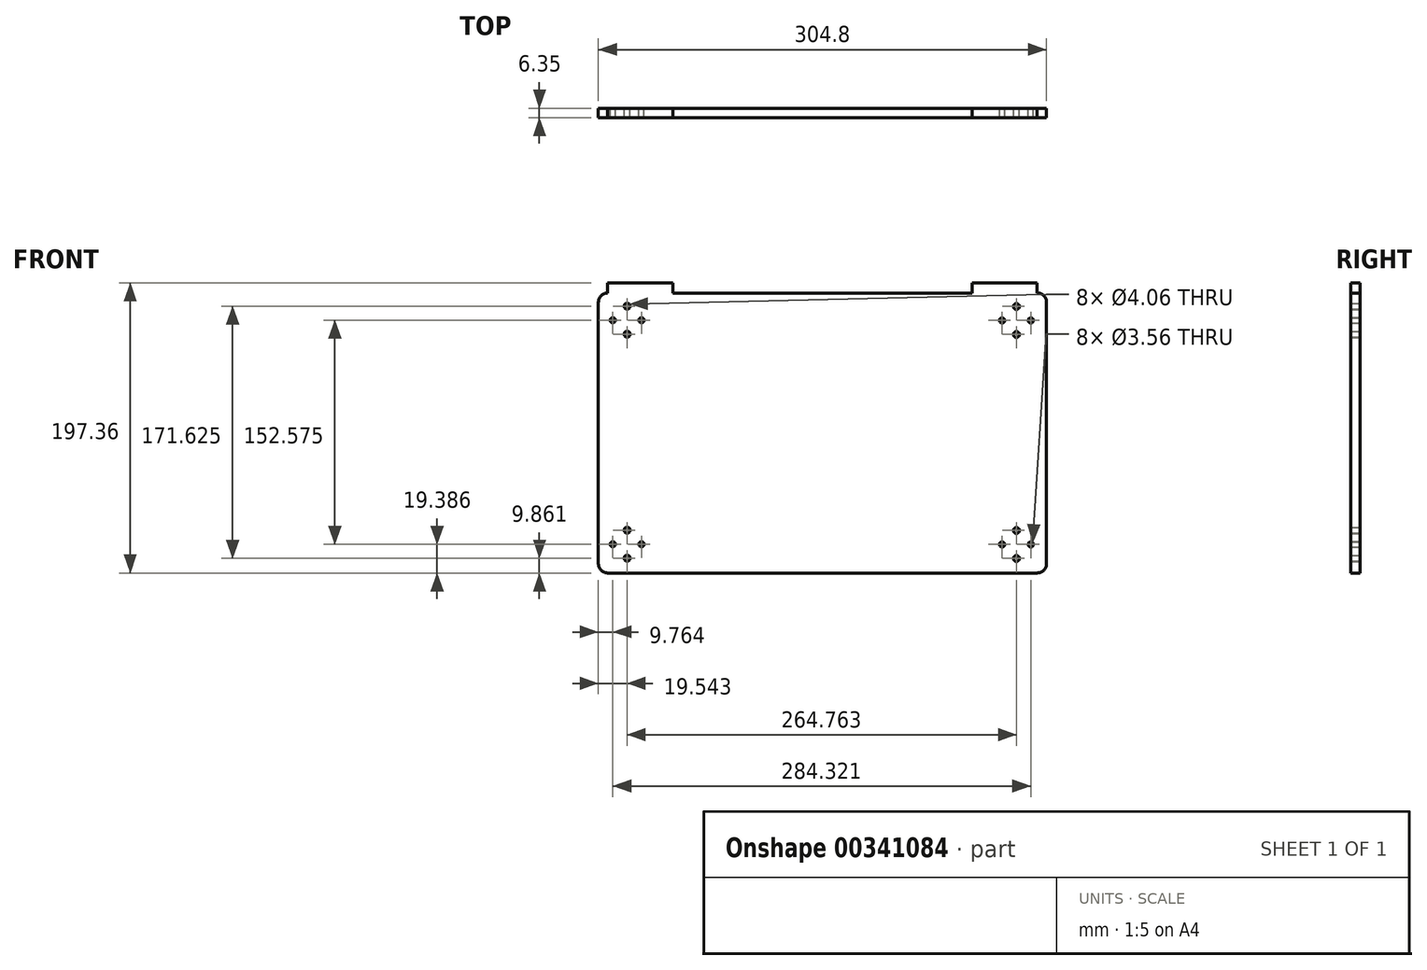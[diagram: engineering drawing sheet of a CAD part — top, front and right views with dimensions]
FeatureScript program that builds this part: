
annotation { "Feature Type Name" : "Feature", "Feature Type Description" : "" }
export const myFeature = defineFeature(function(context is Context, id is Id, definition is map)
    precondition{}
    {
        {
            var Q0;
            Q0=qCreatedBy(makeId("Front.planeOp"),FACE);
            var sketch = newSketch(context, id + "F0", { "sketchPlane" : qUnion([Q0])});
            skLineSegment(sketch, "E0.bottom", {"start": v(-252.66, 148.81) * mm, "end": v(-252.66, 148.81) * mm});
            skLineSegment(sketch, "E0.top", {"start": v(-252.66, -41.69) * mm, "end": v(39.44, -41.69) * mm});
            skLineSegment(sketch, "E0.left", {"start": v(-259, 142.46) * mm, "end": v(-259, -35.34) * mm});
            skLineSegment(sketch, "E0.right", {"start": v(45.8, 142.46) * mm, "end": v(45.8, -35.34) * mm});
            skLineSegment(sketch, "E1.top", {"start": v(-252.66, 155.67) * mm, "end": v(-208.36, 155.67) * mm});
            skLineSegment(sketch, "E1.left", {"start": v(-252.66, 148.81) * mm, "end": v(-252.66, 155.67) * mm});
            skLineSegment(sketch, "E1.right", {"start": v(-208.36, 148.81) * mm, "end": v(-208.36, 155.67) * mm});
            skLineSegment(sketch, "E2.top", {"start": v(39.44, 155.67) * mm, "end": v(-4.86, 155.67) * mm});
            skLineSegment(sketch, "E2.left", {"start": v(39.44, 148.81) * mm, "end": v(39.44, 155.67) * mm});
            skLineSegment(sketch, "E3.trimOffspring", {"start": v(39.44, 148.81) * mm, "end": v(39.44, 148.81) * mm});
            skLineSegment(sketch, "E4.trimOffspring", {"start": v(-208.36, 148.81) * mm, "end": v(-4.86, 148.81) * mm});
            skPoint(sketch, "E5.visualSharp", {"position": v(-259, 148.81) * mm});
            skArc(sketch, "E5.filletArc", {"start": v(-252.66, 148.81) * mm, "mid": v(-257.15, 146.95) * mm, "end": v(-259, 142.46) * mm});
            skPoint(sketch, "E6.visualSharp", {"position": v(-259, -41.69) * mm});
            skArc(sketch, "E6.filletArc", {"start": v(-259, -35.34) * mm, "mid": v(-257.15, -39.83) * mm, "end": v(-252.66, -41.69) * mm});
            skPoint(sketch, "E7.visualSharp", {"position": v(45.8, -41.69) * mm});
            skArc(sketch, "E7.filletArc", {"start": v(39.44, -41.69) * mm, "mid": v(43.93, -39.83) * mm, "end": v(45.8, -35.34) * mm});
            skPoint(sketch, "E8.visualSharp", {"position": v(45.8, 148.81) * mm});
            skArc(sketch, "E8.filletArc", {"start": v(45.8, 142.46) * mm, "mid": v(43.93, 146.95) * mm, "end": v(39.44, 148.81) * mm});
            skCircle(sketch, "E9.0", {"center": v(-239.47, 139.8) * mm, "radius": 2.03 * mm});
            skCircle(sketch, "E10.0", {"center": v(-249.25, 130.27) * mm, "radius": 1.78 * mm});
            skCircle(sketch, "E11.0", {"center": v(-239.47, 120.75) * mm, "radius": 2.03 * mm});
            skCircle(sketch, "E12.0", {"center": v(-229.69, 130.27) * mm, "radius": 1.78 * mm});
            skCircle(sketch, "E13.0", {"center": v(-239.47, -12.6) * mm, "radius": 2.03 * mm});
            skCircle(sketch, "E14.0", {"center": v(-249.25, -22.13) * mm, "radius": 1.78 * mm});
            skCircle(sketch, "E15.0", {"center": v(-239.47, -31.65) * mm, "radius": 2.03 * mm});
            skCircle(sketch, "E16.0", {"center": v(-229.69, -22.13) * mm, "radius": 1.78 * mm});
            skLineSegment(sketch, "E17", {"start": v(-4.86, 148.81) * mm, "end": v(-4.86, 155.67) * mm});
            skCircle(sketch, "E18.0", {"center": v(25.3, 139.62) * mm, "radius": 2.03 * mm});
            skCircle(sketch, "E19.0", {"center": v(15.52, 130.1) * mm, "radius": 1.78 * mm});
            skCircle(sketch, "E20.0", {"center": v(25.3, 120.57) * mm, "radius": 2.03 * mm});
            skCircle(sketch, "E21.0", {"center": v(35.08, 130.1) * mm, "radius": 1.78 * mm});
            skCircle(sketch, "E22.0", {"center": v(25.3, -12.78) * mm, "radius": 2.03 * mm});
            skCircle(sketch, "E23.0", {"center": v(15.52, -22.3) * mm, "radius": 1.78 * mm});
            skCircle(sketch, "E24.0", {"center": v(25.3, -31.83) * mm, "radius": 2.03 * mm});
            skCircle(sketch, "E25.0", {"center": v(35.08, -22.3) * mm, "radius": 1.78 * mm});
            skSolve(sketch);
        }
        {
            var Q0;
            Q0 = qSketchRegion(id + "F0", true);
            extrude(context, id + "F1", {"entities" : qUnion([Q0]), "depth" : 6.35 * mm});
        }
    });
